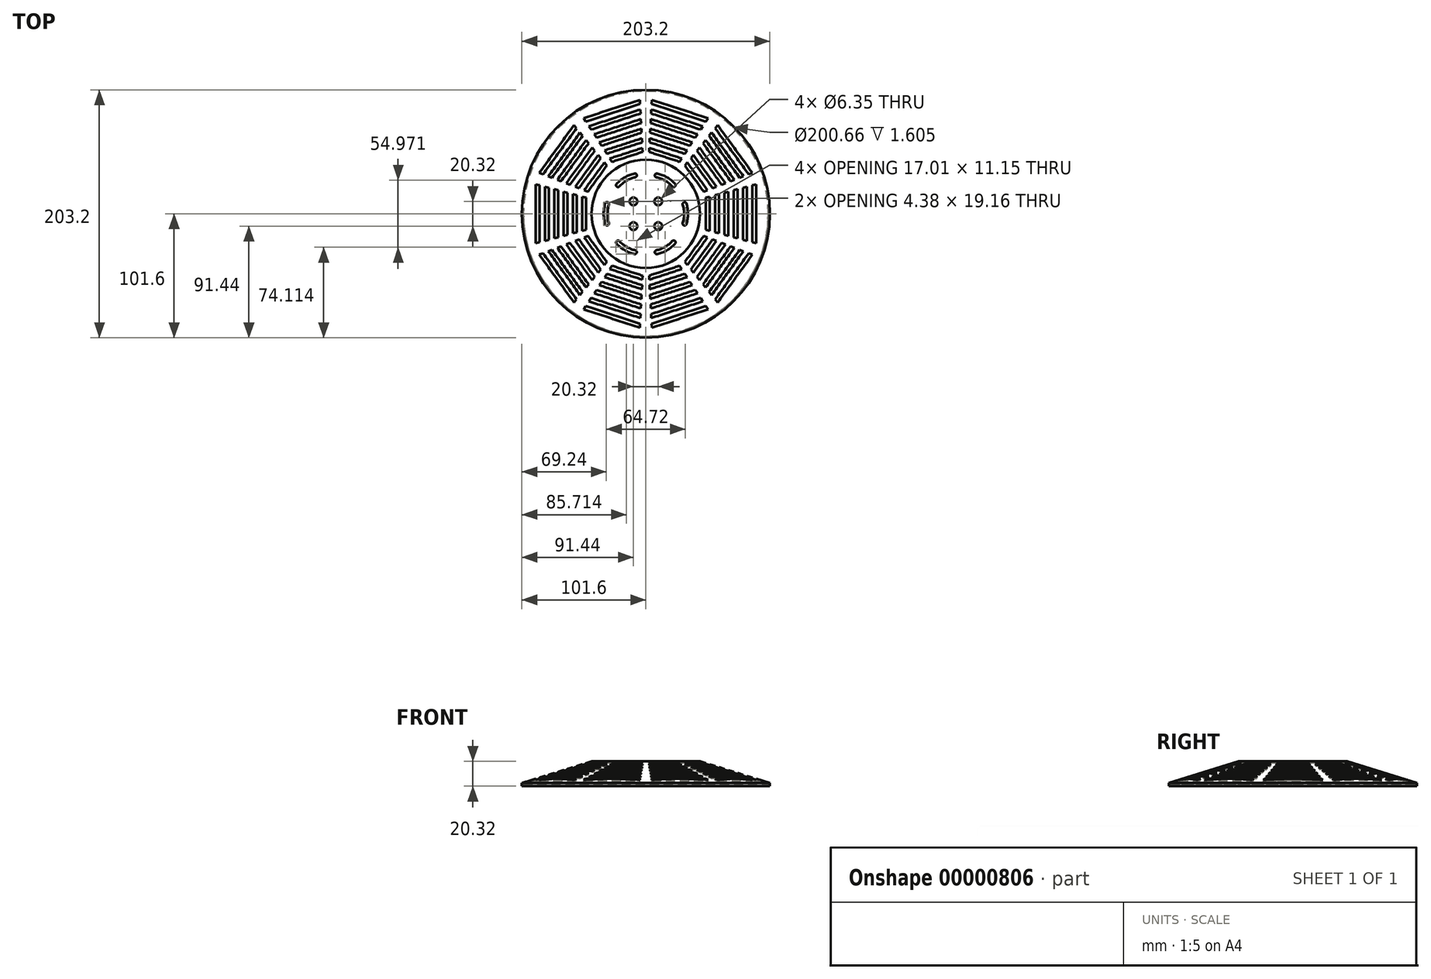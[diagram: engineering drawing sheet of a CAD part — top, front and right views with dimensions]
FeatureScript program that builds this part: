
annotation { "Feature Type Name" : "Feature", "Feature Type Description" : "" }
export const myFeature = defineFeature(function(context is Context, id is Id, definition is map)
    precondition{}
    {
        {
            var Q0;
            Q0=qCreatedBy(makeId("Front.planeOp"),FACE);
            var sketch = newSketch(context, id + "F0", { "sketchPlane" : qUnion([Q0])});
            skLineSegment(sketch, "E0", {"start": v(0, 0) * mm, "end": v(0, 20.32) * mm});
            skLineSegment(sketch, "E1", {"start": v(0, 20.32) * mm, "end": v(44.45, 20.32) * mm});
            skLineSegment(sketch, "E2", {"start": v(44.45, 20.32) * mm, "end": v(101.6, 2.54) * mm});
            skLineSegment(sketch, "E3", {"start": v(101.6, 2.54) * mm, "end": v(101.6, 0) * mm});
            skLineSegment(sketch, "E4", {"start": v(101.6, 0) * mm, "end": v(0, 0) * mm});
            skSolve(sketch);
        }
        {
            var Q0;
            Q0=makeQuery(id+"F0.imprint","IMPRINT",FACE,{"disambiguationData":[TD([[makeQuery(id+"F0.imprint","IMPRINT",EDGE,{"derivedFrom":sQuery(id+"F0.wireOp",EDGE,"E0")}),-1.0]])]});
            var Q1;
            Q1=sQuery(id+"F0.wireOp",EDGE,"E0");
            revolve(context, id + "F1", {"entities" : qUnion([Q0]), "axis" : qUnion([Q1]), "revolveType" : RevolveType.FULL});
        }
        {
            var Q0;
            Q0=makeQuery(id+"F1.opRevolve","SWEPT_FACE",FACE,{"disambiguationData":[OSD([sQuery(id+"F0.wireOp",EDGE,"E4")])]});
            shell(context, id + "F2", {"entities" : qUnion([Q0]), "thickness" : 1.27 * mm});
        }
        {
            var Q0;
            Q0=makeQuery(id+"F1.opRevolve","SWEPT_FACE",FACE,{"disambiguationData":[OSD([sQuery(id+"F0.wireOp",EDGE,"E1")])]});
            var sketch = newSketch(context, id + "F3", { "sketchPlane" : qUnion([Q0])});
            skArc(sketch, "E5", {"start": v(-30.23, 7.53) * mm, "mid": v(-31.38, 0) * mm, "end": v(-30.23, -7.53) * mm});
            skArc(sketch, "E6.0", {"start": v(-33.27, 8.47) * mm, "mid": v(-34.55, 0) * mm, "end": v(-33.27, -8.47) * mm});
            skArc(sketch, "E7", {"start": v(-33.27, -8.47) * mm, "mid": v(-31.28, -9.52) * mm, "end": v(-30.23, -7.53) * mm});
            skArc(sketch, "E8", {"start": v(-30.23, 7.53) * mm, "mid": v(-31.28, 9.52) * mm, "end": v(-33.27, 8.47) * mm});
            skSolve(sketch);
        }
        {
            var Q0;
            Q0=makeQuery(id+"F3.imprint","IMPRINT",FACE,{"disambiguationData":[TD([[makeQuery(id+"F3.imprint","IMPRINT",EDGE,{"derivedFrom":sQuery(id+"F3.wireOp",EDGE,"E5")}),-1.0]])]});
            extrude(context, id + "F4", {"entities" : qUnion([Q0]), "endBound" : BoundingType.THROUGH_ALL, "oppositeDirection" : true, "depth" : 25.4 * mm});
        }
        {
            var Q0;
            Q0=makeQuery(id+"F4.opExtrude","SWEPT_BODY",BODY,{"disambiguationData":[OSD([sQuery(id+"F3.wireOp",EDGE,"E5"),sQuery(id+"F3.wireOp",EDGE,"E6.0"),sQuery(id+"F3.wireOp",EDGE,"E7"),sQuery(id+"F3.wireOp",EDGE,"E8")])]});
            var Q1;
            Q1=makeQuery(id+"F1.opRevolve","SWEPT_EDGE",EDGE,{"disambiguationData":[OSD([sQuery(id+"F0.wireOp",EDGE,"E2"),sQuery(id+"F0.wireOp",EDGE,"E3")])]});
            circularPattern(context, id + "F5", {"entities" : qUnion([Q0]), "axis" : qUnion([Q1]), "angle" : 360 * degree, "instanceCount" : 6, "equalSpace" : true});
        }
        {
            var Q0;
            Q0=makeQuery(id+"F4.opExtrude","SWEPT_BODY",BODY,{"disambiguationData":[OSD([sQuery(id+"F3.wireOp",EDGE,"E5"),sQuery(id+"F3.wireOp",EDGE,"E6.0"),sQuery(id+"F3.wireOp",EDGE,"E7"),sQuery(id+"F3.wireOp",EDGE,"E8")])]});
            var Q1;
            Q1=makeQuery(id+"F5.opPattern","COPY",BODY,{"derivedFrom":makeQuery(id+"F4.opExtrude","SWEPT_BODY",BODY,{"disambiguationData":[OSD([sQuery(id+"F3.wireOp",EDGE,"E5"),sQuery(id+"F3.wireOp",EDGE,"E6.0"),sQuery(id+"F3.wireOp",EDGE,"E7"),sQuery(id+"F3.wireOp",EDGE,"E8")])]}),"instanceName":"1"});
            var Q2;
            Q2=makeQuery(id+"F5.opPattern","COPY",BODY,{"derivedFrom":makeQuery(id+"F4.opExtrude","SWEPT_BODY",BODY,{"disambiguationData":[OSD([sQuery(id+"F3.wireOp",EDGE,"E5"),sQuery(id+"F3.wireOp",EDGE,"E6.0"),sQuery(id+"F3.wireOp",EDGE,"E7"),sQuery(id+"F3.wireOp",EDGE,"E8")])]}),"instanceName":"2"});
            var Q3;
            Q3=makeQuery(id+"F5.opPattern","COPY",BODY,{"derivedFrom":makeQuery(id+"F4.opExtrude","SWEPT_BODY",BODY,{"disambiguationData":[OSD([sQuery(id+"F3.wireOp",EDGE,"E5"),sQuery(id+"F3.wireOp",EDGE,"E6.0"),sQuery(id+"F3.wireOp",EDGE,"E7"),sQuery(id+"F3.wireOp",EDGE,"E8")])]}),"instanceName":"3"});
            var Q4;
            Q4=makeQuery(id+"F5.opPattern","COPY",BODY,{"derivedFrom":makeQuery(id+"F4.opExtrude","SWEPT_BODY",BODY,{"disambiguationData":[OSD([sQuery(id+"F3.wireOp",EDGE,"E5"),sQuery(id+"F3.wireOp",EDGE,"E6.0"),sQuery(id+"F3.wireOp",EDGE,"E7"),sQuery(id+"F3.wireOp",EDGE,"E8")])]}),"instanceName":"4"});
            var Q5;
            Q5=makeQuery(id+"F5.opPattern","COPY",BODY,{"derivedFrom":makeQuery(id+"F4.opExtrude","SWEPT_BODY",BODY,{"disambiguationData":[OSD([sQuery(id+"F3.wireOp",EDGE,"E5"),sQuery(id+"F3.wireOp",EDGE,"E6.0"),sQuery(id+"F3.wireOp",EDGE,"E7"),sQuery(id+"F3.wireOp",EDGE,"E8")])]}),"instanceName":"5"});
            var Q6;
            Q6=makeQuery(id+"F1.opRevolve","SWEPT_BODY",BODY,{"disambiguationData":[OSD([sQuery(id+"F0.wireOp",EDGE,"E0"),sQuery(id+"F0.wireOp",EDGE,"E1"),sQuery(id+"F0.wireOp",EDGE,"E2"),sQuery(id+"F0.wireOp",EDGE,"E3"),sQuery(id+"F0.wireOp",EDGE,"E4")])]});
            booleanBodies(context, id + "F6", {"operationType" : BooleanOperationType.SUBTRACTION, "tools" : qUnion([Q0, Q1, Q2, Q3, Q4, Q5]), "targets" : qUnion([Q6])});
        }
        {
            var Q0;
            Q0=makeQuery(id+"F1.opRevolve","SWEPT_FACE",FACE,{"disambiguationData":[OSD([sQuery(id+"F0.wireOp",EDGE,"E1")])]});
            var sketch = newSketch(context, id + "F7", { "sketchPlane" : qUnion([Q0])});
            skLineSegment(sketch, "E9", {"start": v(0, 0) * mm, "end": v(-98.14, 26.3) * mm});
            skLineSegment(sketch, "E10", {"start": v(0, 0) * mm, "end": v(-98.14, -26.3) * mm});
            skLineSegment(sketch, "E11", {"start": v(-49.07, -13.15) * mm, "end": v(-49.07, 13.15) * mm});
            skLineSegment(sketch, "E12", {"start": v(-52.24, -14) * mm, "end": v(-52.24, 14) * mm});
            skLineSegment(sketch, "E13", {"start": v(-56.69, -15.19) * mm, "end": v(-56.69, 15.19) * mm});
            skLineSegment(sketch, "E14", {"start": v(-59.86, -16.04) * mm, "end": v(-59.86, 16.04) * mm});
            skLineSegment(sketch, "E15", {"start": v(-64.3, -17.23) * mm, "end": v(-64.3, 17.23) * mm});
            skLineSegment(sketch, "E16", {"start": v(-67.48, -18.08) * mm, "end": v(-67.48, 18.08) * mm});
            skLineSegment(sketch, "E17", {"start": v(-71.93, -19.27) * mm, "end": v(-71.93, 19.27) * mm});
            skLineSegment(sketch, "E18", {"start": v(-75.1, -20.12) * mm, "end": v(-75.1, 20.12) * mm});
            skLineSegment(sketch, "E19", {"start": v(-79.55, -21.32) * mm, "end": v(-79.55, 21.32) * mm});
            skLineSegment(sketch, "E20", {"start": v(-82.72, -22.17) * mm, "end": v(-82.72, 22.17) * mm});
            skLineSegment(sketch, "E21", {"start": v(-87.17, -23.36) * mm, "end": v(-87.17, 23.36) * mm});
            skLineSegment(sketch, "E22", {"start": v(-90.34, -24.2) * mm, "end": v(-90.34, 24.2) * mm});
            skSolve(sketch);
        }
        {
            var Q0;
            {var subQ0=sQuery(id+"F7.wireOp",EDGE,"E19");Q0=makeQuery(id+"F7.imprint","IMPRINT",FACE,{"disambiguationData":[TD([[makeQuery(id+"F7.imprint","IMPRINT",EDGE,{"derivedFrom":subQ0}),1.0]])]});}
            var Q1;
            {var subQ0=sQuery(id+"F7.wireOp",EDGE,"E17");Q1=makeQuery(id+"F7.imprint","IMPRINT",FACE,{"disambiguationData":[TD([[makeQuery(id+"F7.imprint","IMPRINT",EDGE,{"derivedFrom":subQ0}),1.0]])]});}
            var Q2;
            {var subQ1=sQuery(id+"F7.wireOp",EDGE,"E15");Q2=makeQuery(id+"F7.imprint","IMPRINT",FACE,{"disambiguationData":[TD([[makeQuery(id+"F7.imprint","IMPRINT",EDGE,{"derivedFrom":subQ1}),1.0]])]});}
            var Q3;
            {var subQ1=sQuery(id+"F7.wireOp",EDGE,"E13");Q3=makeQuery(id+"F7.imprint","IMPRINT",FACE,{"disambiguationData":[TD([[makeQuery(id+"F7.imprint","IMPRINT",EDGE,{"derivedFrom":subQ1}),1.0]])]});}
            var Q4;
            {var subQ0=sQuery(id+"F7.wireOp",EDGE,"E11");Q4=makeQuery(id+"F7.imprint","IMPRINT",FACE,{"disambiguationData":[TD([[makeQuery(id+"F7.imprint","IMPRINT",EDGE,{"derivedFrom":subQ0}),1.0]])]});}
            var Q5;
            {var subQ1=sQuery(id+"F7.wireOp",EDGE,"E21");Q5=makeQuery(id+"F7.imprint","IMPRINT",FACE,{"disambiguationData":[TD([[makeQuery(id+"F7.imprint","IMPRINT",EDGE,{"derivedFrom":subQ1}),1.0]])]});}
            extrude(context, id + "F8", {"entities" : qUnion([Q0, Q1, Q2, Q3, Q4, Q5]), "oppositeDirection" : true, "depth" : 25.4 * mm});
        }
        {
            var Q0;
            Q0=makeQuery(id+"F8.opExtrude","SWEPT_BODY",BODY,{"disambiguationData":[OSD([sQuery(id+"F7.wireOp",EDGE,"E9"),sQuery(id+"F7.wireOp",EDGE,"E10"),sQuery(id+"F7.wireOp",EDGE,"E21"),sQuery(id+"F7.wireOp",EDGE,"E22")])]});
            var Q1;
            Q1=makeQuery(id+"F8.opExtrude","SWEPT_BODY",BODY,{"disambiguationData":[OSD([sQuery(id+"F7.wireOp",EDGE,"E9"),sQuery(id+"F7.wireOp",EDGE,"E10"),sQuery(id+"F7.wireOp",EDGE,"E19"),sQuery(id+"F7.wireOp",EDGE,"E20")])]});
            var Q2;
            Q2=makeQuery(id+"F8.opExtrude","SWEPT_BODY",BODY,{"disambiguationData":[OSD([sQuery(id+"F7.wireOp",EDGE,"E9"),sQuery(id+"F7.wireOp",EDGE,"E10"),sQuery(id+"F7.wireOp",EDGE,"E17"),sQuery(id+"F7.wireOp",EDGE,"E18")])]});
            var Q3;
            Q3=makeQuery(id+"F8.opExtrude","SWEPT_BODY",BODY,{"disambiguationData":[OSD([sQuery(id+"F7.wireOp",EDGE,"E9"),sQuery(id+"F7.wireOp",EDGE,"E10"),sQuery(id+"F7.wireOp",EDGE,"E15"),sQuery(id+"F7.wireOp",EDGE,"E16")])]});
            var Q4;
            Q4=makeQuery(id+"F8.opExtrude","SWEPT_BODY",BODY,{"disambiguationData":[OSD([sQuery(id+"F7.wireOp",EDGE,"E9"),sQuery(id+"F7.wireOp",EDGE,"E10"),sQuery(id+"F7.wireOp",EDGE,"E13"),sQuery(id+"F7.wireOp",EDGE,"E14")])]});
            var Q5;
            Q5=makeQuery(id+"F8.opExtrude","SWEPT_BODY",BODY,{"disambiguationData":[OSD([sQuery(id+"F7.wireOp",EDGE,"E9"),sQuery(id+"F7.wireOp",EDGE,"E10"),sQuery(id+"F7.wireOp",EDGE,"E11"),sQuery(id+"F7.wireOp",EDGE,"E12")])]});
            var Q6;
            Q6=makeQuery(id+"F1.opRevolve","SWEPT_EDGE",EDGE,{"disambiguationData":[OSD([sQuery(id+"F0.wireOp",EDGE,"E2"),sQuery(id+"F0.wireOp",EDGE,"E3")])]});
            circularPattern(context, id + "F9", {"entities" : qUnion([Q0, Q1, Q2, Q3, Q4, Q5]), "axis" : qUnion([Q6]), "angle" : 360 * degree, "instanceCount" : 10, "equalSpace" : true});
        }
        {
            var Q0;
            Q0=makeQuery(id+"F8.opExtrude","SWEPT_BODY",BODY,{"disambiguationData":[OSD([sQuery(id+"F7.wireOp",EDGE,"E9"),sQuery(id+"F7.wireOp",EDGE,"E10"),sQuery(id+"F7.wireOp",EDGE,"E21"),sQuery(id+"F7.wireOp",EDGE,"E22")])]});
            var Q1;
            Q1=makeQuery(id+"F8.opExtrude","SWEPT_BODY",BODY,{"disambiguationData":[OSD([sQuery(id+"F7.wireOp",EDGE,"E9"),sQuery(id+"F7.wireOp",EDGE,"E10"),sQuery(id+"F7.wireOp",EDGE,"E11"),sQuery(id+"F7.wireOp",EDGE,"E12")])]});
            var Q2;
            Q2=makeQuery(id+"F8.opExtrude","SWEPT_BODY",BODY,{"disambiguationData":[OSD([sQuery(id+"F7.wireOp",EDGE,"E9"),sQuery(id+"F7.wireOp",EDGE,"E10"),sQuery(id+"F7.wireOp",EDGE,"E13"),sQuery(id+"F7.wireOp",EDGE,"E14")])]});
            var Q3;
            Q3=makeQuery(id+"F8.opExtrude","SWEPT_BODY",BODY,{"disambiguationData":[OSD([sQuery(id+"F7.wireOp",EDGE,"E9"),sQuery(id+"F7.wireOp",EDGE,"E10"),sQuery(id+"F7.wireOp",EDGE,"E15"),sQuery(id+"F7.wireOp",EDGE,"E16")])]});
            var Q4;
            Q4=makeQuery(id+"F8.opExtrude","SWEPT_BODY",BODY,{"disambiguationData":[OSD([sQuery(id+"F7.wireOp",EDGE,"E9"),sQuery(id+"F7.wireOp",EDGE,"E10"),sQuery(id+"F7.wireOp",EDGE,"E17"),sQuery(id+"F7.wireOp",EDGE,"E18")])]});
            var Q5;
            Q5=makeQuery(id+"F8.opExtrude","SWEPT_BODY",BODY,{"disambiguationData":[OSD([sQuery(id+"F7.wireOp",EDGE,"E9"),sQuery(id+"F7.wireOp",EDGE,"E10"),sQuery(id+"F7.wireOp",EDGE,"E19"),sQuery(id+"F7.wireOp",EDGE,"E20")])]});
            var Q6;
            Q6=makeQuery(id+"F9.opPattern","COPY",BODY,{"derivedFrom":makeQuery(id+"F8.opExtrude","SWEPT_BODY",BODY,{"disambiguationData":[OSD([sQuery(id+"F7.wireOp",EDGE,"E9"),sQuery(id+"F7.wireOp",EDGE,"E10"),sQuery(id+"F7.wireOp",EDGE,"E21"),sQuery(id+"F7.wireOp",EDGE,"E22")])]}),"instanceName":"1"});
            var Q7;
            Q7=makeQuery(id+"F9.opPattern","COPY",BODY,{"derivedFrom":makeQuery(id+"F8.opExtrude","SWEPT_BODY",BODY,{"disambiguationData":[OSD([sQuery(id+"F7.wireOp",EDGE,"E9"),sQuery(id+"F7.wireOp",EDGE,"E10"),sQuery(id+"F7.wireOp",EDGE,"E11"),sQuery(id+"F7.wireOp",EDGE,"E12")])]}),"instanceName":"1"});
            var Q8;
            Q8=makeQuery(id+"F9.opPattern","COPY",BODY,{"derivedFrom":makeQuery(id+"F8.opExtrude","SWEPT_BODY",BODY,{"disambiguationData":[OSD([sQuery(id+"F7.wireOp",EDGE,"E9"),sQuery(id+"F7.wireOp",EDGE,"E10"),sQuery(id+"F7.wireOp",EDGE,"E13"),sQuery(id+"F7.wireOp",EDGE,"E14")])]}),"instanceName":"1"});
            var Q9;
            Q9=makeQuery(id+"F9.opPattern","COPY",BODY,{"derivedFrom":makeQuery(id+"F8.opExtrude","SWEPT_BODY",BODY,{"disambiguationData":[OSD([sQuery(id+"F7.wireOp",EDGE,"E9"),sQuery(id+"F7.wireOp",EDGE,"E10"),sQuery(id+"F7.wireOp",EDGE,"E15"),sQuery(id+"F7.wireOp",EDGE,"E16")])]}),"instanceName":"1"});
            var Q10;
            Q10=makeQuery(id+"F9.opPattern","COPY",BODY,{"derivedFrom":makeQuery(id+"F8.opExtrude","SWEPT_BODY",BODY,{"disambiguationData":[OSD([sQuery(id+"F7.wireOp",EDGE,"E9"),sQuery(id+"F7.wireOp",EDGE,"E10"),sQuery(id+"F7.wireOp",EDGE,"E17"),sQuery(id+"F7.wireOp",EDGE,"E18")])]}),"instanceName":"1"});
            var Q11;
            Q11=makeQuery(id+"F9.opPattern","COPY",BODY,{"derivedFrom":makeQuery(id+"F8.opExtrude","SWEPT_BODY",BODY,{"disambiguationData":[OSD([sQuery(id+"F7.wireOp",EDGE,"E9"),sQuery(id+"F7.wireOp",EDGE,"E10"),sQuery(id+"F7.wireOp",EDGE,"E19"),sQuery(id+"F7.wireOp",EDGE,"E20")])]}),"instanceName":"1"});
            var Q12;
            Q12=makeQuery(id+"F9.opPattern","COPY",BODY,{"derivedFrom":makeQuery(id+"F8.opExtrude","SWEPT_BODY",BODY,{"disambiguationData":[OSD([sQuery(id+"F7.wireOp",EDGE,"E9"),sQuery(id+"F7.wireOp",EDGE,"E10"),sQuery(id+"F7.wireOp",EDGE,"E21"),sQuery(id+"F7.wireOp",EDGE,"E22")])]}),"instanceName":"2"});
            var Q13;
            Q13=makeQuery(id+"F9.opPattern","COPY",BODY,{"derivedFrom":makeQuery(id+"F8.opExtrude","SWEPT_BODY",BODY,{"disambiguationData":[OSD([sQuery(id+"F7.wireOp",EDGE,"E9"),sQuery(id+"F7.wireOp",EDGE,"E10"),sQuery(id+"F7.wireOp",EDGE,"E11"),sQuery(id+"F7.wireOp",EDGE,"E12")])]}),"instanceName":"2"});
            var Q14;
            Q14=makeQuery(id+"F9.opPattern","COPY",BODY,{"derivedFrom":makeQuery(id+"F8.opExtrude","SWEPT_BODY",BODY,{"disambiguationData":[OSD([sQuery(id+"F7.wireOp",EDGE,"E9"),sQuery(id+"F7.wireOp",EDGE,"E10"),sQuery(id+"F7.wireOp",EDGE,"E13"),sQuery(id+"F7.wireOp",EDGE,"E14")])]}),"instanceName":"2"});
            var Q15;
            Q15=makeQuery(id+"F9.opPattern","COPY",BODY,{"derivedFrom":makeQuery(id+"F8.opExtrude","SWEPT_BODY",BODY,{"disambiguationData":[OSD([sQuery(id+"F7.wireOp",EDGE,"E9"),sQuery(id+"F7.wireOp",EDGE,"E10"),sQuery(id+"F7.wireOp",EDGE,"E15"),sQuery(id+"F7.wireOp",EDGE,"E16")])]}),"instanceName":"2"});
            var Q16;
            Q16=makeQuery(id+"F9.opPattern","COPY",BODY,{"derivedFrom":makeQuery(id+"F8.opExtrude","SWEPT_BODY",BODY,{"disambiguationData":[OSD([sQuery(id+"F7.wireOp",EDGE,"E9"),sQuery(id+"F7.wireOp",EDGE,"E10"),sQuery(id+"F7.wireOp",EDGE,"E17"),sQuery(id+"F7.wireOp",EDGE,"E18")])]}),"instanceName":"2"});
            var Q17;
            Q17=makeQuery(id+"F9.opPattern","COPY",BODY,{"derivedFrom":makeQuery(id+"F8.opExtrude","SWEPT_BODY",BODY,{"disambiguationData":[OSD([sQuery(id+"F7.wireOp",EDGE,"E9"),sQuery(id+"F7.wireOp",EDGE,"E10"),sQuery(id+"F7.wireOp",EDGE,"E19"),sQuery(id+"F7.wireOp",EDGE,"E20")])]}),"instanceName":"2"});
            var Q18;
            Q18=makeQuery(id+"F9.opPattern","COPY",BODY,{"derivedFrom":makeQuery(id+"F8.opExtrude","SWEPT_BODY",BODY,{"disambiguationData":[OSD([sQuery(id+"F7.wireOp",EDGE,"E9"),sQuery(id+"F7.wireOp",EDGE,"E10"),sQuery(id+"F7.wireOp",EDGE,"E21"),sQuery(id+"F7.wireOp",EDGE,"E22")])]}),"instanceName":"3"});
            var Q19;
            Q19=makeQuery(id+"F9.opPattern","COPY",BODY,{"derivedFrom":makeQuery(id+"F8.opExtrude","SWEPT_BODY",BODY,{"disambiguationData":[OSD([sQuery(id+"F7.wireOp",EDGE,"E9"),sQuery(id+"F7.wireOp",EDGE,"E10"),sQuery(id+"F7.wireOp",EDGE,"E11"),sQuery(id+"F7.wireOp",EDGE,"E12")])]}),"instanceName":"3"});
            var Q20;
            Q20=makeQuery(id+"F9.opPattern","COPY",BODY,{"derivedFrom":makeQuery(id+"F8.opExtrude","SWEPT_BODY",BODY,{"disambiguationData":[OSD([sQuery(id+"F7.wireOp",EDGE,"E9"),sQuery(id+"F7.wireOp",EDGE,"E10"),sQuery(id+"F7.wireOp",EDGE,"E13"),sQuery(id+"F7.wireOp",EDGE,"E14")])]}),"instanceName":"3"});
            var Q21;
            Q21=makeQuery(id+"F9.opPattern","COPY",BODY,{"derivedFrom":makeQuery(id+"F8.opExtrude","SWEPT_BODY",BODY,{"disambiguationData":[OSD([sQuery(id+"F7.wireOp",EDGE,"E9"),sQuery(id+"F7.wireOp",EDGE,"E10"),sQuery(id+"F7.wireOp",EDGE,"E15"),sQuery(id+"F7.wireOp",EDGE,"E16")])]}),"instanceName":"3"});
            var Q22;
            Q22=makeQuery(id+"F9.opPattern","COPY",BODY,{"derivedFrom":makeQuery(id+"F8.opExtrude","SWEPT_BODY",BODY,{"disambiguationData":[OSD([sQuery(id+"F7.wireOp",EDGE,"E9"),sQuery(id+"F7.wireOp",EDGE,"E10"),sQuery(id+"F7.wireOp",EDGE,"E17"),sQuery(id+"F7.wireOp",EDGE,"E18")])]}),"instanceName":"3"});
            var Q23;
            Q23=makeQuery(id+"F9.opPattern","COPY",BODY,{"derivedFrom":makeQuery(id+"F8.opExtrude","SWEPT_BODY",BODY,{"disambiguationData":[OSD([sQuery(id+"F7.wireOp",EDGE,"E9"),sQuery(id+"F7.wireOp",EDGE,"E10"),sQuery(id+"F7.wireOp",EDGE,"E19"),sQuery(id+"F7.wireOp",EDGE,"E20")])]}),"instanceName":"3"});
            var Q24;
            Q24=makeQuery(id+"F9.opPattern","COPY",BODY,{"derivedFrom":makeQuery(id+"F8.opExtrude","SWEPT_BODY",BODY,{"disambiguationData":[OSD([sQuery(id+"F7.wireOp",EDGE,"E9"),sQuery(id+"F7.wireOp",EDGE,"E10"),sQuery(id+"F7.wireOp",EDGE,"E21"),sQuery(id+"F7.wireOp",EDGE,"E22")])]}),"instanceName":"4"});
            var Q25;
            Q25=makeQuery(id+"F9.opPattern","COPY",BODY,{"derivedFrom":makeQuery(id+"F8.opExtrude","SWEPT_BODY",BODY,{"disambiguationData":[OSD([sQuery(id+"F7.wireOp",EDGE,"E9"),sQuery(id+"F7.wireOp",EDGE,"E10"),sQuery(id+"F7.wireOp",EDGE,"E11"),sQuery(id+"F7.wireOp",EDGE,"E12")])]}),"instanceName":"4"});
            var Q26;
            Q26=makeQuery(id+"F9.opPattern","COPY",BODY,{"derivedFrom":makeQuery(id+"F8.opExtrude","SWEPT_BODY",BODY,{"disambiguationData":[OSD([sQuery(id+"F7.wireOp",EDGE,"E9"),sQuery(id+"F7.wireOp",EDGE,"E10"),sQuery(id+"F7.wireOp",EDGE,"E13"),sQuery(id+"F7.wireOp",EDGE,"E14")])]}),"instanceName":"4"});
            var Q27;
            Q27=makeQuery(id+"F9.opPattern","COPY",BODY,{"derivedFrom":makeQuery(id+"F8.opExtrude","SWEPT_BODY",BODY,{"disambiguationData":[OSD([sQuery(id+"F7.wireOp",EDGE,"E9"),sQuery(id+"F7.wireOp",EDGE,"E10"),sQuery(id+"F7.wireOp",EDGE,"E15"),sQuery(id+"F7.wireOp",EDGE,"E16")])]}),"instanceName":"4"});
            var Q28;
            Q28=makeQuery(id+"F9.opPattern","COPY",BODY,{"derivedFrom":makeQuery(id+"F8.opExtrude","SWEPT_BODY",BODY,{"disambiguationData":[OSD([sQuery(id+"F7.wireOp",EDGE,"E9"),sQuery(id+"F7.wireOp",EDGE,"E10"),sQuery(id+"F7.wireOp",EDGE,"E17"),sQuery(id+"F7.wireOp",EDGE,"E18")])]}),"instanceName":"4"});
            var Q29;
            Q29=makeQuery(id+"F9.opPattern","COPY",BODY,{"derivedFrom":makeQuery(id+"F8.opExtrude","SWEPT_BODY",BODY,{"disambiguationData":[OSD([sQuery(id+"F7.wireOp",EDGE,"E9"),sQuery(id+"F7.wireOp",EDGE,"E10"),sQuery(id+"F7.wireOp",EDGE,"E19"),sQuery(id+"F7.wireOp",EDGE,"E20")])]}),"instanceName":"4"});
            var Q30;
            Q30=makeQuery(id+"F9.opPattern","COPY",BODY,{"derivedFrom":makeQuery(id+"F8.opExtrude","SWEPT_BODY",BODY,{"disambiguationData":[OSD([sQuery(id+"F7.wireOp",EDGE,"E9"),sQuery(id+"F7.wireOp",EDGE,"E10"),sQuery(id+"F7.wireOp",EDGE,"E21"),sQuery(id+"F7.wireOp",EDGE,"E22")])]}),"instanceName":"5"});
            var Q31;
            Q31=makeQuery(id+"F9.opPattern","COPY",BODY,{"derivedFrom":makeQuery(id+"F8.opExtrude","SWEPT_BODY",BODY,{"disambiguationData":[OSD([sQuery(id+"F7.wireOp",EDGE,"E9"),sQuery(id+"F7.wireOp",EDGE,"E10"),sQuery(id+"F7.wireOp",EDGE,"E11"),sQuery(id+"F7.wireOp",EDGE,"E12")])]}),"instanceName":"5"});
            var Q32;
            Q32=makeQuery(id+"F9.opPattern","COPY",BODY,{"derivedFrom":makeQuery(id+"F8.opExtrude","SWEPT_BODY",BODY,{"disambiguationData":[OSD([sQuery(id+"F7.wireOp",EDGE,"E9"),sQuery(id+"F7.wireOp",EDGE,"E10"),sQuery(id+"F7.wireOp",EDGE,"E13"),sQuery(id+"F7.wireOp",EDGE,"E14")])]}),"instanceName":"5"});
            var Q33;
            Q33=makeQuery(id+"F9.opPattern","COPY",BODY,{"derivedFrom":makeQuery(id+"F8.opExtrude","SWEPT_BODY",BODY,{"disambiguationData":[OSD([sQuery(id+"F7.wireOp",EDGE,"E9"),sQuery(id+"F7.wireOp",EDGE,"E10"),sQuery(id+"F7.wireOp",EDGE,"E15"),sQuery(id+"F7.wireOp",EDGE,"E16")])]}),"instanceName":"5"});
            var Q34;
            Q34=makeQuery(id+"F9.opPattern","COPY",BODY,{"derivedFrom":makeQuery(id+"F8.opExtrude","SWEPT_BODY",BODY,{"disambiguationData":[OSD([sQuery(id+"F7.wireOp",EDGE,"E9"),sQuery(id+"F7.wireOp",EDGE,"E10"),sQuery(id+"F7.wireOp",EDGE,"E17"),sQuery(id+"F7.wireOp",EDGE,"E18")])]}),"instanceName":"5"});
            var Q35;
            Q35=makeQuery(id+"F9.opPattern","COPY",BODY,{"derivedFrom":makeQuery(id+"F8.opExtrude","SWEPT_BODY",BODY,{"disambiguationData":[OSD([sQuery(id+"F7.wireOp",EDGE,"E9"),sQuery(id+"F7.wireOp",EDGE,"E10"),sQuery(id+"F7.wireOp",EDGE,"E19"),sQuery(id+"F7.wireOp",EDGE,"E20")])]}),"instanceName":"5"});
            var Q36;
            Q36=makeQuery(id+"F9.opPattern","COPY",BODY,{"derivedFrom":makeQuery(id+"F8.opExtrude","SWEPT_BODY",BODY,{"disambiguationData":[OSD([sQuery(id+"F7.wireOp",EDGE,"E9"),sQuery(id+"F7.wireOp",EDGE,"E10"),sQuery(id+"F7.wireOp",EDGE,"E21"),sQuery(id+"F7.wireOp",EDGE,"E22")])]}),"instanceName":"6"});
            var Q37;
            Q37=makeQuery(id+"F9.opPattern","COPY",BODY,{"derivedFrom":makeQuery(id+"F8.opExtrude","SWEPT_BODY",BODY,{"disambiguationData":[OSD([sQuery(id+"F7.wireOp",EDGE,"E9"),sQuery(id+"F7.wireOp",EDGE,"E10"),sQuery(id+"F7.wireOp",EDGE,"E11"),sQuery(id+"F7.wireOp",EDGE,"E12")])]}),"instanceName":"6"});
            var Q38;
            Q38=makeQuery(id+"F9.opPattern","COPY",BODY,{"derivedFrom":makeQuery(id+"F8.opExtrude","SWEPT_BODY",BODY,{"disambiguationData":[OSD([sQuery(id+"F7.wireOp",EDGE,"E9"),sQuery(id+"F7.wireOp",EDGE,"E10"),sQuery(id+"F7.wireOp",EDGE,"E13"),sQuery(id+"F7.wireOp",EDGE,"E14")])]}),"instanceName":"6"});
            var Q39;
            Q39=makeQuery(id+"F9.opPattern","COPY",BODY,{"derivedFrom":makeQuery(id+"F8.opExtrude","SWEPT_BODY",BODY,{"disambiguationData":[OSD([sQuery(id+"F7.wireOp",EDGE,"E9"),sQuery(id+"F7.wireOp",EDGE,"E10"),sQuery(id+"F7.wireOp",EDGE,"E15"),sQuery(id+"F7.wireOp",EDGE,"E16")])]}),"instanceName":"6"});
            var Q40;
            Q40=makeQuery(id+"F9.opPattern","COPY",BODY,{"derivedFrom":makeQuery(id+"F8.opExtrude","SWEPT_BODY",BODY,{"disambiguationData":[OSD([sQuery(id+"F7.wireOp",EDGE,"E9"),sQuery(id+"F7.wireOp",EDGE,"E10"),sQuery(id+"F7.wireOp",EDGE,"E17"),sQuery(id+"F7.wireOp",EDGE,"E18")])]}),"instanceName":"6"});
            var Q41;
            Q41=makeQuery(id+"F9.opPattern","COPY",BODY,{"derivedFrom":makeQuery(id+"F8.opExtrude","SWEPT_BODY",BODY,{"disambiguationData":[OSD([sQuery(id+"F7.wireOp",EDGE,"E9"),sQuery(id+"F7.wireOp",EDGE,"E10"),sQuery(id+"F7.wireOp",EDGE,"E19"),sQuery(id+"F7.wireOp",EDGE,"E20")])]}),"instanceName":"6"});
            var Q42;
            Q42=makeQuery(id+"F9.opPattern","COPY",BODY,{"derivedFrom":makeQuery(id+"F8.opExtrude","SWEPT_BODY",BODY,{"disambiguationData":[OSD([sQuery(id+"F7.wireOp",EDGE,"E9"),sQuery(id+"F7.wireOp",EDGE,"E10"),sQuery(id+"F7.wireOp",EDGE,"E21"),sQuery(id+"F7.wireOp",EDGE,"E22")])]}),"instanceName":"7"});
            var Q43;
            Q43=makeQuery(id+"F9.opPattern","COPY",BODY,{"derivedFrom":makeQuery(id+"F8.opExtrude","SWEPT_BODY",BODY,{"disambiguationData":[OSD([sQuery(id+"F7.wireOp",EDGE,"E9"),sQuery(id+"F7.wireOp",EDGE,"E10"),sQuery(id+"F7.wireOp",EDGE,"E11"),sQuery(id+"F7.wireOp",EDGE,"E12")])]}),"instanceName":"7"});
            var Q44;
            Q44=makeQuery(id+"F9.opPattern","COPY",BODY,{"derivedFrom":makeQuery(id+"F8.opExtrude","SWEPT_BODY",BODY,{"disambiguationData":[OSD([sQuery(id+"F7.wireOp",EDGE,"E9"),sQuery(id+"F7.wireOp",EDGE,"E10"),sQuery(id+"F7.wireOp",EDGE,"E13"),sQuery(id+"F7.wireOp",EDGE,"E14")])]}),"instanceName":"7"});
            var Q45;
            Q45=makeQuery(id+"F9.opPattern","COPY",BODY,{"derivedFrom":makeQuery(id+"F8.opExtrude","SWEPT_BODY",BODY,{"disambiguationData":[OSD([sQuery(id+"F7.wireOp",EDGE,"E9"),sQuery(id+"F7.wireOp",EDGE,"E10"),sQuery(id+"F7.wireOp",EDGE,"E15"),sQuery(id+"F7.wireOp",EDGE,"E16")])]}),"instanceName":"7"});
            var Q46;
            Q46=makeQuery(id+"F9.opPattern","COPY",BODY,{"derivedFrom":makeQuery(id+"F8.opExtrude","SWEPT_BODY",BODY,{"disambiguationData":[OSD([sQuery(id+"F7.wireOp",EDGE,"E9"),sQuery(id+"F7.wireOp",EDGE,"E10"),sQuery(id+"F7.wireOp",EDGE,"E17"),sQuery(id+"F7.wireOp",EDGE,"E18")])]}),"instanceName":"7"});
            var Q47;
            Q47=makeQuery(id+"F9.opPattern","COPY",BODY,{"derivedFrom":makeQuery(id+"F8.opExtrude","SWEPT_BODY",BODY,{"disambiguationData":[OSD([sQuery(id+"F7.wireOp",EDGE,"E9"),sQuery(id+"F7.wireOp",EDGE,"E10"),sQuery(id+"F7.wireOp",EDGE,"E19"),sQuery(id+"F7.wireOp",EDGE,"E20")])]}),"instanceName":"7"});
            var Q48;
            Q48=makeQuery(id+"F9.opPattern","COPY",BODY,{"derivedFrom":makeQuery(id+"F8.opExtrude","SWEPT_BODY",BODY,{"disambiguationData":[OSD([sQuery(id+"F7.wireOp",EDGE,"E9"),sQuery(id+"F7.wireOp",EDGE,"E10"),sQuery(id+"F7.wireOp",EDGE,"E21"),sQuery(id+"F7.wireOp",EDGE,"E22")])]}),"instanceName":"8"});
            var Q49;
            Q49=makeQuery(id+"F9.opPattern","COPY",BODY,{"derivedFrom":makeQuery(id+"F8.opExtrude","SWEPT_BODY",BODY,{"disambiguationData":[OSD([sQuery(id+"F7.wireOp",EDGE,"E9"),sQuery(id+"F7.wireOp",EDGE,"E10"),sQuery(id+"F7.wireOp",EDGE,"E11"),sQuery(id+"F7.wireOp",EDGE,"E12")])]}),"instanceName":"8"});
            var Q50;
            Q50=makeQuery(id+"F9.opPattern","COPY",BODY,{"derivedFrom":makeQuery(id+"F8.opExtrude","SWEPT_BODY",BODY,{"disambiguationData":[OSD([sQuery(id+"F7.wireOp",EDGE,"E9"),sQuery(id+"F7.wireOp",EDGE,"E10"),sQuery(id+"F7.wireOp",EDGE,"E13"),sQuery(id+"F7.wireOp",EDGE,"E14")])]}),"instanceName":"8"});
            var Q51;
            Q51=makeQuery(id+"F9.opPattern","COPY",BODY,{"derivedFrom":makeQuery(id+"F8.opExtrude","SWEPT_BODY",BODY,{"disambiguationData":[OSD([sQuery(id+"F7.wireOp",EDGE,"E9"),sQuery(id+"F7.wireOp",EDGE,"E10"),sQuery(id+"F7.wireOp",EDGE,"E15"),sQuery(id+"F7.wireOp",EDGE,"E16")])]}),"instanceName":"8"});
            var Q52;
            Q52=makeQuery(id+"F9.opPattern","COPY",BODY,{"derivedFrom":makeQuery(id+"F8.opExtrude","SWEPT_BODY",BODY,{"disambiguationData":[OSD([sQuery(id+"F7.wireOp",EDGE,"E9"),sQuery(id+"F7.wireOp",EDGE,"E10"),sQuery(id+"F7.wireOp",EDGE,"E17"),sQuery(id+"F7.wireOp",EDGE,"E18")])]}),"instanceName":"8"});
            var Q53;
            Q53=makeQuery(id+"F9.opPattern","COPY",BODY,{"derivedFrom":makeQuery(id+"F8.opExtrude","SWEPT_BODY",BODY,{"disambiguationData":[OSD([sQuery(id+"F7.wireOp",EDGE,"E9"),sQuery(id+"F7.wireOp",EDGE,"E10"),sQuery(id+"F7.wireOp",EDGE,"E19"),sQuery(id+"F7.wireOp",EDGE,"E20")])]}),"instanceName":"8"});
            var Q54;
            Q54=makeQuery(id+"F9.opPattern","COPY",BODY,{"derivedFrom":makeQuery(id+"F8.opExtrude","SWEPT_BODY",BODY,{"disambiguationData":[OSD([sQuery(id+"F7.wireOp",EDGE,"E9"),sQuery(id+"F7.wireOp",EDGE,"E10"),sQuery(id+"F7.wireOp",EDGE,"E21"),sQuery(id+"F7.wireOp",EDGE,"E22")])]}),"instanceName":"9"});
            var Q55;
            Q55=makeQuery(id+"F9.opPattern","COPY",BODY,{"derivedFrom":makeQuery(id+"F8.opExtrude","SWEPT_BODY",BODY,{"disambiguationData":[OSD([sQuery(id+"F7.wireOp",EDGE,"E9"),sQuery(id+"F7.wireOp",EDGE,"E10"),sQuery(id+"F7.wireOp",EDGE,"E11"),sQuery(id+"F7.wireOp",EDGE,"E12")])]}),"instanceName":"9"});
            var Q56;
            Q56=makeQuery(id+"F9.opPattern","COPY",BODY,{"derivedFrom":makeQuery(id+"F8.opExtrude","SWEPT_BODY",BODY,{"disambiguationData":[OSD([sQuery(id+"F7.wireOp",EDGE,"E9"),sQuery(id+"F7.wireOp",EDGE,"E10"),sQuery(id+"F7.wireOp",EDGE,"E13"),sQuery(id+"F7.wireOp",EDGE,"E14")])]}),"instanceName":"9"});
            var Q57;
            Q57=makeQuery(id+"F9.opPattern","COPY",BODY,{"derivedFrom":makeQuery(id+"F8.opExtrude","SWEPT_BODY",BODY,{"disambiguationData":[OSD([sQuery(id+"F7.wireOp",EDGE,"E9"),sQuery(id+"F7.wireOp",EDGE,"E10"),sQuery(id+"F7.wireOp",EDGE,"E15"),sQuery(id+"F7.wireOp",EDGE,"E16")])]}),"instanceName":"9"});
            var Q58;
            Q58=makeQuery(id+"F9.opPattern","COPY",BODY,{"derivedFrom":makeQuery(id+"F8.opExtrude","SWEPT_BODY",BODY,{"disambiguationData":[OSD([sQuery(id+"F7.wireOp",EDGE,"E9"),sQuery(id+"F7.wireOp",EDGE,"E10"),sQuery(id+"F7.wireOp",EDGE,"E17"),sQuery(id+"F7.wireOp",EDGE,"E18")])]}),"instanceName":"9"});
            var Q59;
            Q59=makeQuery(id+"F9.opPattern","COPY",BODY,{"derivedFrom":makeQuery(id+"F8.opExtrude","SWEPT_BODY",BODY,{"disambiguationData":[OSD([sQuery(id+"F7.wireOp",EDGE,"E9"),sQuery(id+"F7.wireOp",EDGE,"E10"),sQuery(id+"F7.wireOp",EDGE,"E19"),sQuery(id+"F7.wireOp",EDGE,"E20")])]}),"instanceName":"9"});
            var Q60;
            Q60=makeQuery(id+"F1.opRevolve","SWEPT_BODY",BODY,{"disambiguationData":[OSD([sQuery(id+"F0.wireOp",EDGE,"E0"),sQuery(id+"F0.wireOp",EDGE,"E1"),sQuery(id+"F0.wireOp",EDGE,"E2"),sQuery(id+"F0.wireOp",EDGE,"E3"),sQuery(id+"F0.wireOp",EDGE,"E4")])]});
            booleanBodies(context, id + "F10", {"operationType" : BooleanOperationType.SUBTRACTION, "tools" : qUnion([Q0, Q1, Q2, Q3, Q4, Q5, Q6, Q7, Q8, Q9, Q10, Q11, Q12, Q13, Q14, Q15, Q16, Q17, Q18, Q19, Q20, Q21, Q22, Q23, Q24, Q25, Q26, Q27, Q28, Q29, Q30, Q31, Q32, Q33, Q34, Q35, Q36, Q37, Q38, Q39, Q40, Q41, Q42, Q43, Q44, Q45, Q46, Q47, Q48, Q49, Q50, Q51, Q52, Q53, Q54, Q55, Q56, Q57, Q58, Q59]), "targets" : qUnion([Q60])});
        }
        {
            var Q0;
            Q0=makeQuery(id+"F1.opRevolve","SWEPT_FACE",FACE,{"disambiguationData":[OSD([sQuery(id+"F0.wireOp",EDGE,"E1")])]});
            var sketch = newSketch(context, id + "F11", { "sketchPlane" : qUnion([Q0])});
            skCircle(sketch, "E23", {"center": v(-10.16, -10.16) * mm, "radius": 3.18 * mm});
            skCircle(sketch, "E24", {"center": v(-10.16, 10.16) * mm, "radius": 3.18 * mm});
            skCircle(sketch, "E25", {"center": v(10.16, -10.16) * mm, "radius": 3.18 * mm});
            skCircle(sketch, "E26", {"center": v(10.16, 10.16) * mm, "radius": 3.18 * mm});
            skSolve(sketch);
        }
        {
            var Q0;
            {Q0=qUnion([makeQuery(id+"F11.imprint","IMPRINT",FACE,{"disambiguationData":[TD([[makeQuery(id+"F11.imprint","IMPRINT",EDGE,{"derivedFrom":sQuery(id+"F11.wireOp",EDGE,"E23")}),1.0]])]}),makeQuery(id+"F11.imprint","IMPRINT",FACE,{"disambiguationData":[TD([[makeQuery(id+"F11.imprint","IMPRINT",EDGE,{"derivedFrom":sQuery(id+"F11.wireOp",EDGE,"E24")}),1.0]])]}),makeQuery(id+"F11.imprint","IMPRINT",FACE,{"disambiguationData":[TD([[makeQuery(id+"F11.imprint","IMPRINT",EDGE,{"derivedFrom":sQuery(id+"F11.wireOp",EDGE,"E25")}),1.0]])]}),makeQuery(id+"F11.imprint","IMPRINT",FACE,{"disambiguationData":[TD([[makeQuery(id+"F11.imprint","IMPRINT",EDGE,{"derivedFrom":sQuery(id+"F11.wireOp",EDGE,"E26")}),1.0]])]})]);}
            extrude(context, id + "F12", {"entities" : qUnion([Q0]), "operationType" : NewBodyOperationType.REMOVE, "endBound" : BoundingType.THROUGH_ALL, "oppositeDirection" : true, "depth" : 25.4 * mm});
        }
    });
